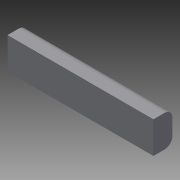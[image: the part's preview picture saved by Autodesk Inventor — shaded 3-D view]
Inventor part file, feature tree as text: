
AUTODESK INVENTOR PART (.ipt)
format: ipt  version: 2013 (Build 170138000, 138)  size: 78,848 bytes
history: native  units: in
note: dims shown in document units (in); Inventor stores cm internally (conversion verified against a paired STEP export)
features: extrude x1, fillet x1, sketch x1
ambient origin geometry x8: Origin, YZ Plane, XZ Plane, XY Plane, X Axis, Y Axis, Z Axis, Center Point
bodies: Solid1 (feature_tree)
feature tree (3):
  extrude  "Extrusion1"  Depth=1.0in
  fillet  "Fillet1"  Radius=5.0in
  sketch  "Sketch1"  dims[d0=3.625in d1=1.0in d2=5.0in d3=0.0in d4=23.0in d5=90.0deg d6=5.0in d7=90.0deg d8=3.0in d9=0.0in d10=1.25in]
